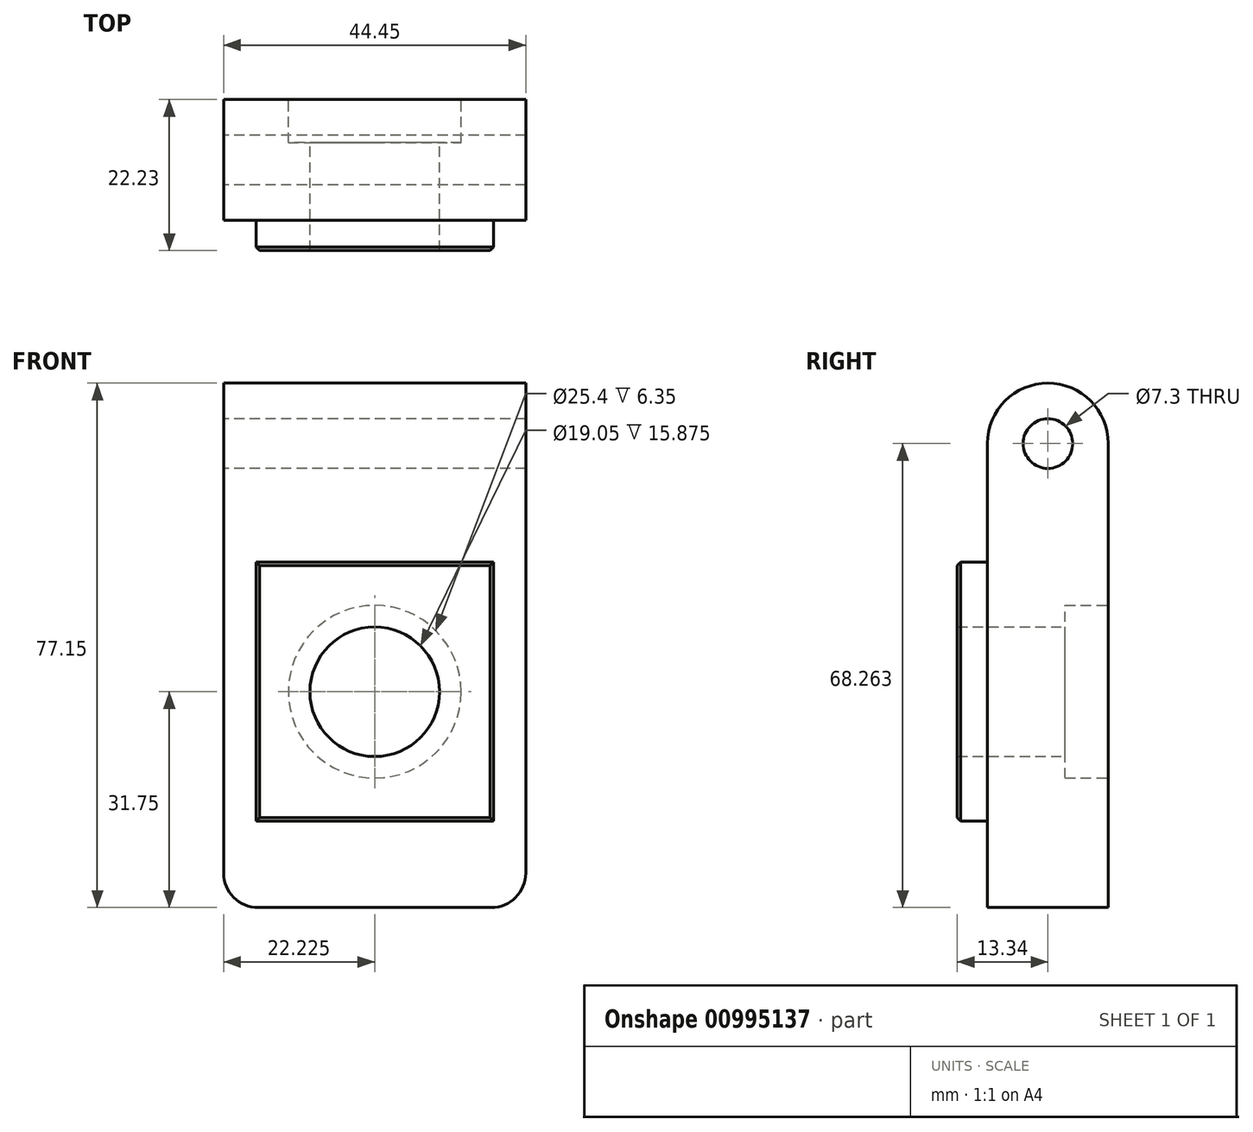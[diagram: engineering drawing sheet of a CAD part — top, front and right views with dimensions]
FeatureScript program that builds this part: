
annotation { "Feature Type Name" : "Feature", "Feature Type Description" : "" }
export const myFeature = defineFeature(function(context is Context, id is Id, definition is map)
    precondition{}
    {
        {
            var Q0;
            Q0=qCreatedBy(makeId("Right.planeOp"),FACE);
            var sketch = newSketch(context, id + "F0", { "sketchPlane" : qUnion([Q0])});
            skLineSegment(sketch, "E0.bottom", {"start": v(0, 0) * mm, "end": v(-17.78, 0) * mm});
            skLineSegment(sketch, "E0.left", {"start": v(0, 0) * mm, "end": v(0, 68.26) * mm});
            skLineSegment(sketch, "E0.right", {"start": v(-17.78, 0) * mm, "end": v(-17.78, 68.26) * mm});
            skLineSegment(sketch, "E1", {"start": v(0, 0) * mm, "end": v(0, -12.7) * mm, "construction": true});
            skLineSegment(sketch, "E2", {"start": v(0, -12.7) * mm, "end": v(-8.9, -12.7) * mm, "construction": true});
            skLineSegment(sketch, "E3", {"start": v(-8.9, -12.7) * mm, "end": v(-8.9, 0) * mm, "construction": true});
            skLineSegment(sketch, "E4", {"start": v(-8.9, 0) * mm, "end": v(-8.9, 68.26) * mm, "construction": true});
            skPoint(sketch, "E5.visualSharp", {"position": v(0, 76.2) * mm});
            skArc(sketch, "E5.filletArc", {"start": v(0, 68.26) * mm, "mid": v(-8.9, 77.15) * mm, "end": v(-17.78, 68.26) * mm});
            skCircle(sketch, "E6", {"center": v(-8.9, 68.26) * mm, "radius": 3.65 * mm});
            skLineSegment(sketch, "E7", {"start": v(-15.18, 74.55) * mm, "end": v(-15.18, 74.55) * mm});
            skSolve(sketch);
        }
        {
            var Q0;
            Q0 = qSketchRegion(id + "F0", true);
            extrude(context, id + "F1", {"entities" : qUnion([Q0]), "depth" : 44.45 * mm, "offsetDistance" : 25.4 * mm});
        }
        {
            var Q0;
            Q0=qCreatedBy(makeId("Front.planeOp"),FACE);
            var sketch = newSketch(context, id + "F2", { "sketchPlane" : qUnion([Q0])});
            skLineSegment(sketch, "E8", {"start": v(0, 0) * mm, "end": v(22.23, 0) * mm, "construction": true});
            skLineSegment(sketch, "E9", {"start": v(22.23, 0) * mm, "end": v(22.23, 31.75) * mm, "construction": true});
            skCircle(sketch, "E10", {"center": v(22.23, 31.75) * mm, "radius": 9.53 * mm});
            skCircle(sketch, "E11", {"center": v(22.23, 31.75) * mm, "radius": 12.7 * mm});
            skSolve(sketch);
        }
        {
            var Q0;
            Q0=qCreatedBy(makeId("Front.planeOp"),FACE);
            var sketch = newSketch(context, id + "F3", { "sketchPlane" : qUnion([Q0])});
            skLineSegment(sketch, "E12", {"start": v(0, 0) * mm, "end": v(22.23, 0) * mm, "construction": true});
            skLineSegment(sketch, "E13", {"start": v(22.23, 0) * mm, "end": v(22.23, 31.75) * mm, "construction": true});
            skLineSegment(sketch, "E14.bottom", {"start": v(39.69, 12.7) * mm, "end": v(4.76, 12.7) * mm});
            skLineSegment(sketch, "E14.top", {"start": v(39.69, 50.8) * mm, "end": v(4.76, 50.8) * mm});
            skLineSegment(sketch, "E14.left", {"start": v(39.69, 12.7) * mm, "end": v(39.69, 50.8) * mm});
            skLineSegment(sketch, "E14.right", {"start": v(4.76, 12.7) * mm, "end": v(4.76, 50.8) * mm});
            skPoint(sketch, "E14.middle", {"position": v(22.23, 31.75) * mm});
            skSolve(sketch);
        }
        {
            var Q0;
            Q0 = qSketchRegion(id + "F3", true);
            extrude(context, id + "F4", {"entities" : qUnion([Q0]), "operationType" : NewBodyOperationType.ADD, "depth" : 22.22 * mm, "offsetDistance" : 25.4 * mm});
        }
        {
            var Q0;
            Q0=makeQuery(id+"F4.opExtrude","CAP_EDGE",EDGE,{"disambiguationData":[OSD([sQuery(id+"F3.wireOp",EDGE,"E14.right")])],"isStart":false});
            var Q1;
            Q1=makeQuery(id+"F4.opExtrude","CAP_EDGE",EDGE,{"disambiguationData":[OSD([sQuery(id+"F3.wireOp",EDGE,"E14.top")])],"isStart":false});
            var Q2;
            Q2=makeQuery(id+"F4.opExtrude","CAP_EDGE",EDGE,{"disambiguationData":[OSD([sQuery(id+"F3.wireOp",EDGE,"E14.bottom")])],"isStart":false});
            var Q3;
            Q3=makeQuery(id+"F4.opExtrude","CAP_EDGE",EDGE,{"disambiguationData":[OSD([sQuery(id+"F3.wireOp",EDGE,"E14.left")])],"isStart":false});
            chamfer(context, id + "F5", {"entities" : qUnion([Q0, Q1, Q2, Q3]), "width" : 0.5 * mm, "tangentPropagation" : true});
        }
        {
            var Q0;
            Q0=makeQuery(id+"F2.imprint","IMPRINT",FACE,{"disambiguationData":[TD([[makeQuery(id+"F2.imprint","IMPRINT",EDGE,{"derivedFrom":sQuery(id+"F2.wireOp",EDGE,"E10")}),-1.0]])]});
            extrude(context, id + "F6", {"entities" : qUnion([Q0]), "operationType" : NewBodyOperationType.REMOVE, "depth" : 6.35 * mm, "offsetDistance" : 25.4 * mm});
        }
        {
            var Q0;
            Q0=makeQuery(id+"F2.imprint","IMPRINT",FACE,{"disambiguationData":[TD([[makeQuery(id+"F2.imprint","IMPRINT",EDGE,{"derivedFrom":sQuery(id+"F2.wireOp",EDGE,"E10")}),1.0]])]});
            extrude(context, id + "F7", {"entities" : qUnion([Q0]), "operationType" : NewBodyOperationType.REMOVE, "depth" : 25.4 * mm, "offsetDistance" : 25.4 * mm});
        }
        {
            var Q0;
            Q0=makeQuery(id+"F1.opExtrude","CAP_EDGE",EDGE,{"disambiguationData":[OSD([sQuery(id+"F0.wireOp",EDGE,"E0.bottom")])],"isStart":true});
            var Q1;
            Q1=makeQuery(id+"F1.opExtrude","CAP_EDGE",EDGE,{"disambiguationData":[OSD([sQuery(id+"F0.wireOp",EDGE,"E0.bottom")])],"isStart":false});
            fillet(context, id + "F8", {"entities" : qUnion([Q0, Q1]), "radius" : 5.08 * mm, "tangentPropagation" : true, "allowEdgeOverflow" : false});
        }
    });
